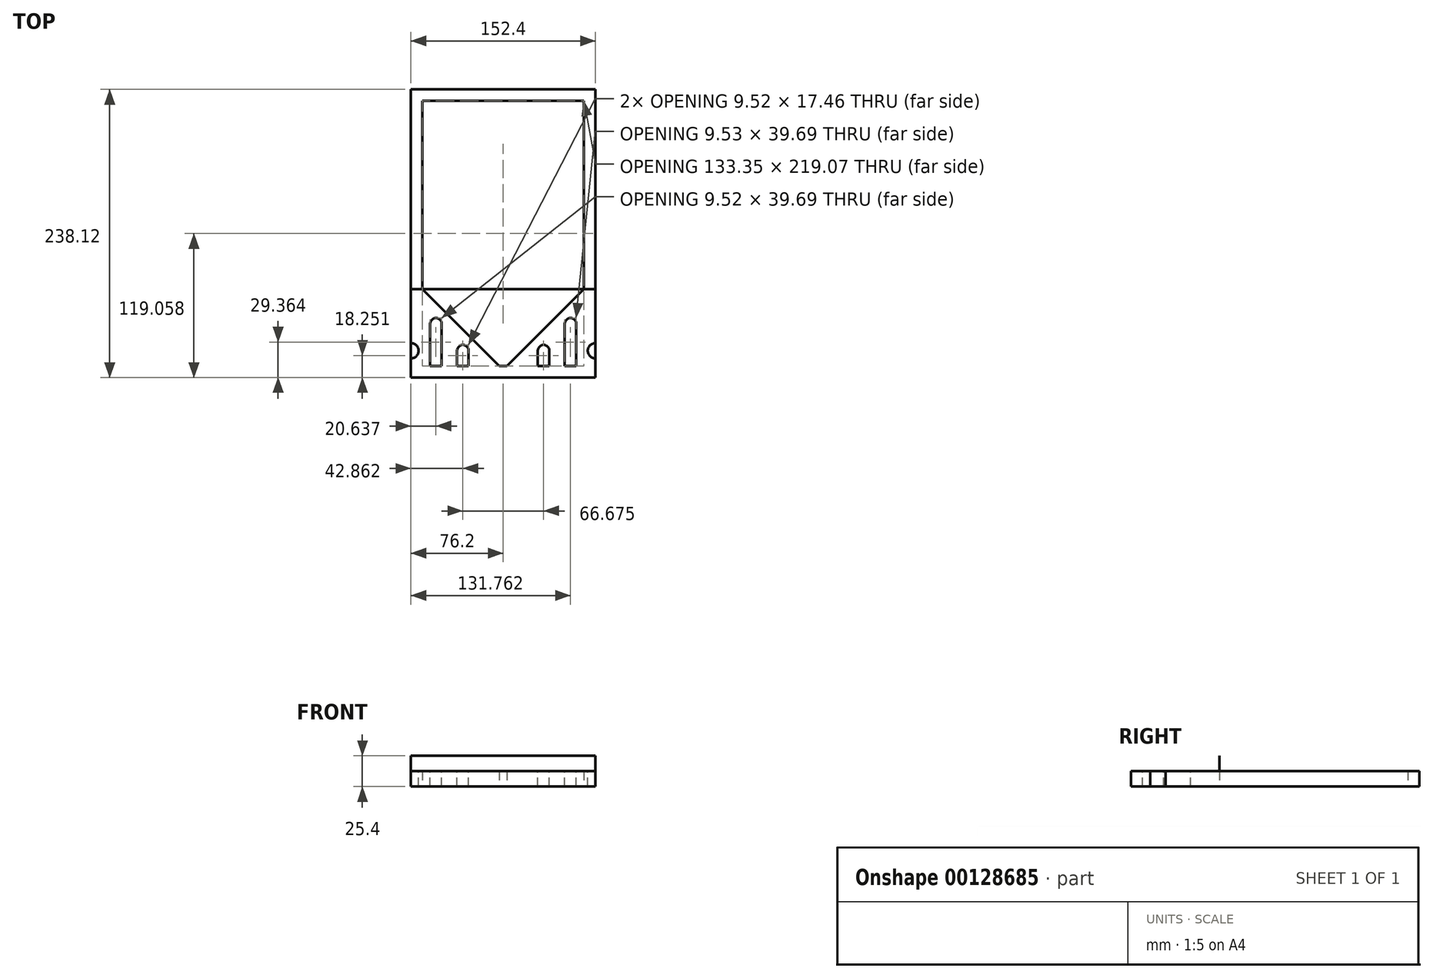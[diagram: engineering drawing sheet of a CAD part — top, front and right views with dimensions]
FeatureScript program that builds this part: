
annotation { "Feature Type Name" : "Feature", "Feature Type Description" : "" }
export const myFeature = defineFeature(function(context is Context, id is Id, definition is map)
    precondition{}
    {
        {
            var Q0;
            Q0=qCreatedBy(makeId("Top.planeOp"),FACE);
            var sketch = newSketch(context, id + "F0", { "sketchPlane" : qUnion([Q0])});
            skLineSegment(sketch, "E0", {"start": v(0, 0) * mm, "end": v(0, -238.13) * mm});
            skLineSegment(sketch, "E1", {"start": v(0, -238.13) * mm, "end": v(152.4, -238.13) * mm});
            skLineSegment(sketch, "E2", {"start": v(152.4, -238.13) * mm, "end": v(152.4, 0) * mm});
            skLineSegment(sketch, "E3", {"start": v(152.4, 0) * mm, "end": v(0, 0) * mm});
            skLineSegment(sketch, "E4.1", {"start": v(142.87, -9.53) * mm, "end": v(9.53, -9.53) * mm});
            skLineSegment(sketch, "E5", {"start": v(73.03, -228.6) * mm, "end": v(9.53, -165.1) * mm});
            skLineSegment(sketch, "E6", {"start": v(9.53, -165.1) * mm, "end": v(9.53, -9.53) * mm});
            skLineSegment(sketch, "E7", {"start": v(142.87, -9.53) * mm, "end": v(142.87, -165.1) * mm});
            skLineSegment(sketch, "E8.MirrorCS", {"start": v(79.38, -228.6) * mm, "end": v(142.87, -165.1) * mm});
            skLineSegment(sketch, "E9", {"start": v(73.03, -228.6) * mm, "end": v(79.38, -228.6) * mm});
            skSolve(sketch);
        }
        {
            var Q0;
            Q0=makeQuery(id+"F0.imprint","IMPRINT",FACE,{"disambiguationData":[TD([[makeQuery(id+"F0.imprint","IMPRINT",EDGE,{"derivedFrom":sQuery(id+"F0.wireOp",EDGE,"E0")}),1.0]])]});
            extrude(context, id + "F1", {"entities" : qUnion([Q0]), "depth" : 12.7 * mm});
        }
        {
            var Q0;
            Q0=makeQuery(id+"F1.opExtrude","CAP_FACE",FACE,{"disambiguationData":[OSD([sQuery(id+"F0.wireOp",EDGE,"E0"),sQuery(id+"F0.wireOp",EDGE,"E1"),sQuery(id+"F0.wireOp",EDGE,"E2"),sQuery(id+"F0.wireOp",EDGE,"E3"),sQuery(id+"F0.wireOp",EDGE,"E4.1"),sQuery(id+"F0.wireOp",EDGE,"E5"),sQuery(id+"F0.wireOp",EDGE,"E6"),sQuery(id+"F0.wireOp",EDGE,"E7"),sQuery(id+"F0.wireOp",EDGE,"E8.MirrorCS"),sQuery(id+"F0.wireOp",EDGE,"E9")])],"isStart":false});
            var sketch = newSketch(context, id + "F2", { "sketchPlane" : qUnion([Q0])});
            skArc(sketch, "E10", {"start": v(0, -222.25) * mm, "mid": v(6.35, -215.9) * mm, "end": v(0, -209.55) * mm});
            skLineSegment(sketch, "E11", {"start": v(0, -222.25) * mm, "end": v(0, -209.55) * mm});
            skPoint(sketch, "E12.endSnap0", {"position": v(76.2, -228.6) * mm});
            skLineSegment(sketch, "E13", {"start": v(152.4, -222.25) * mm, "end": v(152.4, -209.55) * mm});
            skArc(sketch, "E14", {"start": v(152.4, -209.55) * mm, "mid": v(146.05, -215.9) * mm, "end": v(152.4, -222.25) * mm});
            skSolve(sketch);
        }
        {
            var Q0;
            Q0 = qSketchRegion(id + "F2", true);
            extrude(context, id + "F3", {"entities" : qUnion([Q0]), "operationType" : NewBodyOperationType.REMOVE, "endBound" : BoundingType.UP_TO_NEXT, "oppositeDirection" : true, "depth" : 25.4 * mm});
        }
        {
            var Q0;
            Q0=makeQuery(id+"F1.opExtrude","CAP_FACE",FACE,{"disambiguationData":[OSD([sQuery(id+"F0.wireOp",EDGE,"E0"),sQuery(id+"F0.wireOp",EDGE,"E1"),sQuery(id+"F0.wireOp",EDGE,"E2"),sQuery(id+"F0.wireOp",EDGE,"E3"),sQuery(id+"F0.wireOp",EDGE,"E4.1"),sQuery(id+"F0.wireOp",EDGE,"E5"),sQuery(id+"F0.wireOp",EDGE,"E6"),sQuery(id+"F0.wireOp",EDGE,"E7"),sQuery(id+"F0.wireOp",EDGE,"E8.MirrorCS"),sQuery(id+"F0.wireOp",EDGE,"E9")])],"isStart":false});
            var sketch = newSketch(context, id + "F4", { "sketchPlane" : qUnion([Q0])});
            skLineSegment(sketch, "E15", {"start": v(15.88, -228.6) * mm, "end": v(25.4, -228.6) * mm});
            skLineSegment(sketch, "E16", {"start": v(38.1, -228.6) * mm, "end": v(47.62, -228.6) * mm});
            skLineSegment(sketch, "E17", {"start": v(47.62, -228.6) * mm, "end": v(47.62, -215.9) * mm});
            skLineSegment(sketch, "E18", {"start": v(38.1, -228.6) * mm, "end": v(38.1, -215.9) * mm});
            skLineSegment(sketch, "E19", {"start": v(15.88, -228.6) * mm, "end": v(15.88, -193.68) * mm});
            skLineSegment(sketch, "E20", {"start": v(25.4, -193.68) * mm, "end": v(25.4, -228.6) * mm});
            skArc(sketch, "E21", {"start": v(25.4, -193.68) * mm, "mid": v(20.64, -188.91) * mm, "end": v(15.88, -193.68) * mm});
            skArc(sketch, "E22", {"start": v(47.62, -215.9) * mm, "mid": v(42.86, -211.14) * mm, "end": v(38.1, -215.9) * mm});
            skArc(sketch, "E23.MirrorCS", {"start": v(127, -193.68) * mm, "mid": v(131.76, -188.91) * mm, "end": v(136.53, -193.68) * mm});
            skLineSegment(sketch, "E24.MirrorCS", {"start": v(127, -193.68) * mm, "end": v(127, -228.6) * mm});
            skLineSegment(sketch, "E25.MirrorCS", {"start": v(136.53, -228.6) * mm, "end": v(136.53, -193.68) * mm});
            skLineSegment(sketch, "E26.MirrorCS", {"start": v(136.53, -228.6) * mm, "end": v(127, -228.6) * mm});
            skLineSegment(sketch, "E27.MirrorCS", {"start": v(104.78, -228.6) * mm, "end": v(104.78, -215.9) * mm});
            skArc(sketch, "E28.MirrorCS", {"start": v(104.78, -215.9) * mm, "mid": v(109.54, -211.14) * mm, "end": v(114.3, -215.9) * mm});
            skLineSegment(sketch, "E29.MirrorCS", {"start": v(114.3, -228.6) * mm, "end": v(104.78, -228.6) * mm});
            skLineSegment(sketch, "E30.MirrorCS", {"start": v(114.3, -228.6) * mm, "end": v(114.3, -215.9) * mm});
            skSolve(sketch);
        }
        {
            var Q0;
            Q0 = qSketchRegion(id + "F4", true);
            extrude(context, id + "F5", {"entities" : qUnion([Q0]), "operationType" : NewBodyOperationType.REMOVE, "oppositeDirection" : true, "depth" : 25.4 * mm});
        }
        {
            var Q0;
            Q0=makeQuery(id+"F1.opExtrude","CAP_FACE",FACE,{"disambiguationData":[OSD([sQuery(id+"F0.wireOp",EDGE,"E0"),sQuery(id+"F0.wireOp",EDGE,"E1"),sQuery(id+"F0.wireOp",EDGE,"E2"),sQuery(id+"F0.wireOp",EDGE,"E3"),sQuery(id+"F0.wireOp",EDGE,"E4.1"),sQuery(id+"F0.wireOp",EDGE,"E5"),sQuery(id+"F0.wireOp",EDGE,"E6"),sQuery(id+"F0.wireOp",EDGE,"E7"),sQuery(id+"F0.wireOp",EDGE,"E8.MirrorCS"),sQuery(id+"F0.wireOp",EDGE,"E9")])],"isStart":false});
            var sketch = newSketch(context, id + "F6", { "sketchPlane" : qUnion([Q0])});
            skLineSegment(sketch, "E31.0", {"start": v(9.53, -165.1) * mm, "end": v(9.53, -9.53) * mm});
            skLineSegment(sketch, "E31.1", {"start": v(73.03, -228.6) * mm, "end": v(9.53, -165.1) * mm});
            skLineSegment(sketch, "E31.2", {"start": v(73.03, -228.6) * mm, "end": v(79.38, -228.6) * mm});
            skLineSegment(sketch, "E31.3", {"start": v(79.38, -228.6) * mm, "end": v(142.87, -165.1) * mm});
            skLineSegment(sketch, "E31.4", {"start": v(142.87, -9.53) * mm, "end": v(142.87, -165.1) * mm});
            skLineSegment(sketch, "E31.5", {"start": v(142.87, -9.53) * mm, "end": v(9.53, -9.53) * mm});
            skLineSegment(sketch, "E32.0", {"start": v(15.88, -228.6) * mm, "end": v(15.88, -193.68) * mm});
            skLineSegment(sketch, "E32.1", {"start": v(25.4, -193.68) * mm, "end": v(25.4, -228.6) * mm});
            skLineSegment(sketch, "E32.2", {"start": v(15.88, -228.6) * mm, "end": v(25.4, -228.6) * mm});
            skArc(sketch, "E32.3", {"start": v(25.4, -193.68) * mm, "mid": v(20.64, -188.91) * mm, "end": v(15.88, -193.68) * mm});
            skArc(sketch, "E32.4", {"start": v(47.62, -215.9) * mm, "mid": v(42.86, -211.14) * mm, "end": v(38.1, -215.9) * mm});
            skLineSegment(sketch, "E32.5", {"start": v(38.1, -228.6) * mm, "end": v(38.1, -215.9) * mm});
            skLineSegment(sketch, "E32.6", {"start": v(38.1, -228.6) * mm, "end": v(47.62, -228.6) * mm});
            skLineSegment(sketch, "E32.7", {"start": v(47.62, -228.6) * mm, "end": v(47.62, -215.9) * mm});
            skLineSegment(sketch, "E32.8", {"start": v(104.78, -228.6) * mm, "end": v(104.78, -215.9) * mm});
            skArc(sketch, "E32.9", {"start": v(104.78, -215.9) * mm, "mid": v(109.54, -211.14) * mm, "end": v(114.3, -215.9) * mm});
            skLineSegment(sketch, "E32.10", {"start": v(114.3, -228.6) * mm, "end": v(114.3, -215.9) * mm});
            skLineSegment(sketch, "E32.11", {"start": v(114.3, -228.6) * mm, "end": v(104.78, -228.6) * mm});
            skLineSegment(sketch, "E32.12", {"start": v(127, -193.68) * mm, "end": v(127, -228.6) * mm});
            skLineSegment(sketch, "E32.13", {"start": v(136.53, -228.6) * mm, "end": v(136.53, -193.68) * mm});
            skLineSegment(sketch, "E32.14", {"start": v(136.53, -228.6) * mm, "end": v(127, -228.6) * mm});
            skArc(sketch, "E32.15", {"start": v(127, -193.68) * mm, "mid": v(131.76, -188.91) * mm, "end": v(136.53, -193.68) * mm});
            skSolve(sketch);
        }
        {
            var Q0;
            Q0 = qSketchRegion(id + "F6", true);
            extrude(context, id + "F7", {"entities" : qUnion([Q0]), "oppositeDirection" : true, "depth" : 12.7 * mm});
        }
        {
            var Q0;
            Q0=makeQuery(id+"F1.opExtrude","CAP_FACE",FACE,{"disambiguationData":[OSD([sQuery(id+"F0.wireOp",EDGE,"E0"),sQuery(id+"F0.wireOp",EDGE,"E1"),sQuery(id+"F0.wireOp",EDGE,"E2"),sQuery(id+"F0.wireOp",EDGE,"E3"),sQuery(id+"F0.wireOp",EDGE,"E4.1"),sQuery(id+"F0.wireOp",EDGE,"E5"),sQuery(id+"F0.wireOp",EDGE,"E6"),sQuery(id+"F0.wireOp",EDGE,"E7"),sQuery(id+"F0.wireOp",EDGE,"E8.MirrorCS"),sQuery(id+"F0.wireOp",EDGE,"E9")])],"isStart":false});
            var sketch = newSketch(context, id + "F8", { "sketchPlane" : qUnion([Q0])});
            skArc(sketch, "E33.0", {"start": v(0, -222.25) * mm, "mid": v(6.35, -215.9) * mm, "end": v(0, -209.55) * mm});
            skArc(sketch, "E33.1", {"start": v(152.4, -209.55) * mm, "mid": v(146.05, -215.9) * mm, "end": v(152.4, -222.25) * mm});
            skLineSegment(sketch, "E34", {"start": v(0, -222.25) * mm, "end": v(0, -209.55) * mm});
            skLineSegment(sketch, "E35", {"start": v(152.4, -209.55) * mm, "end": v(152.4, -222.25) * mm});
            skSolve(sketch);
        }
        {
            var Q0;
            Q0 = qSketchRegion(id + "F8", true);
            extrude(context, id + "F9", {"entities" : qUnion([Q0]), "oppositeDirection" : true, "depth" : 12.7 * mm});
        }
        {
            var Q0;
            Q0=makeQuery(id+"F1.opExtrude","CAP_FACE",FACE,{"disambiguationData":[OSD([sQuery(id+"F0.wireOp",EDGE,"E0"),sQuery(id+"F0.wireOp",EDGE,"E1"),sQuery(id+"F0.wireOp",EDGE,"E2"),sQuery(id+"F0.wireOp",EDGE,"E3"),sQuery(id+"F0.wireOp",EDGE,"E4.1"),sQuery(id+"F0.wireOp",EDGE,"E5"),sQuery(id+"F0.wireOp",EDGE,"E6"),sQuery(id+"F0.wireOp",EDGE,"E7"),sQuery(id+"F0.wireOp",EDGE,"E8.MirrorCS"),sQuery(id+"F0.wireOp",EDGE,"E9")])],"isStart":false});
            var sketch = newSketch(context, id + "F10", { "sketchPlane" : qUnion([Q0])});
            skLineSegment(sketch, "E36", {"start": v(0, -165.1) * mm, "end": v(152.4, -165.1) * mm});
            skSolve(sketch);
        }
        {
            var Q0;
            Q0=sQuery(id+"F10.wireOp",EDGE,"E36");
            extrude(context, id + "F11", {"bodyType" : ToolBodyType.SURFACE, "surfaceEntities" : qUnion([Q0]), "depth" : 12.7 * mm});
        }
        {
            var Q0;
            Q0=makeQuery(id+"F11.opExtrude","SWEPT_FACE",FACE,{"disambiguationData":[OSD([sQuery(id+"F10.wireOp",EDGE,"E36")])]});
            extrude(context, id + "F12", {"entities" : qUnion([Q0]), "depth" : 0.01 * mm});
        }
    });
